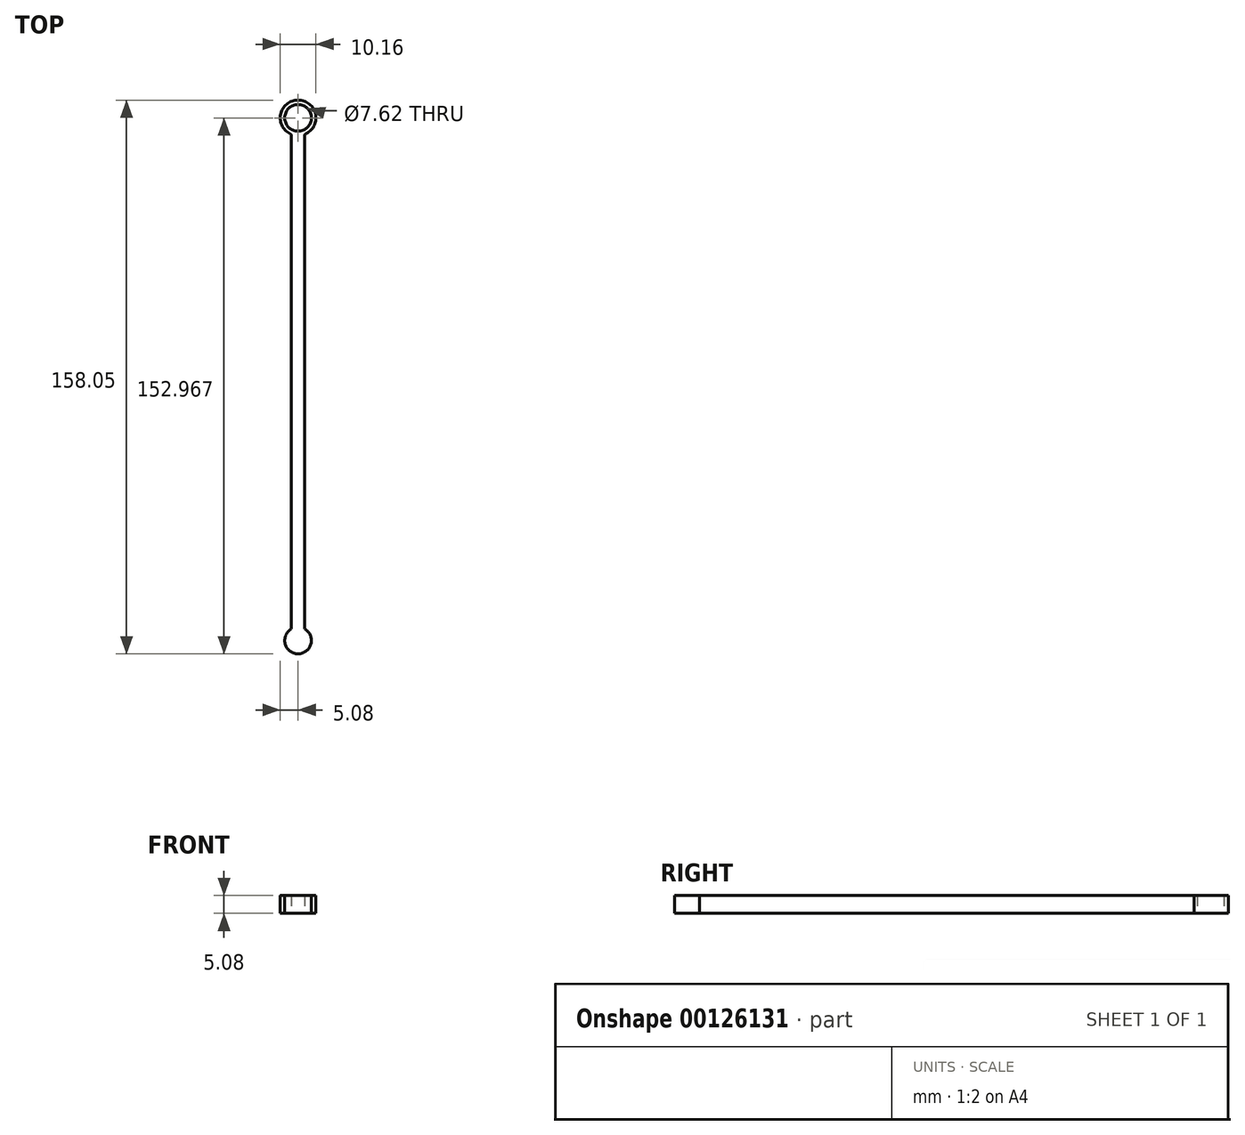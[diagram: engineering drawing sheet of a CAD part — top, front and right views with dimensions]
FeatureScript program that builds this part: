
annotation { "Feature Type Name" : "Feature", "Feature Type Description" : "" }
export const myFeature = defineFeature(function(context is Context, id is Id, definition is map)
    precondition{}
    {
        {
            var Q0;
            Q0=qCreatedBy(makeId("Top.planeOp"),FACE);
            var sketch = newSketch(context, id + "F0", { "sketchPlane" : qUnion([Q0])});
            skCircle(sketch, "E0", {"center": v(0, 45.97) * mm, "radius": 5.08 * mm});
            skLineSegment(sketch, "E1.bottom", {"start": v(-1.9, 40.32) * mm, "end": v(1.9, 40.32) * mm});
            skLineSegment(sketch, "E1.top", {"start": v(-1.9, -99.38) * mm, "end": v(1.9, -99.38) * mm});
            skLineSegment(sketch, "E1.left", {"start": v(-1.9, 40.32) * mm, "end": v(-1.9, -99.38) * mm});
            skLineSegment(sketch, "E1.right", {"start": v(1.9, 40.32) * mm, "end": v(1.9, -99.38) * mm});
            skCircle(sketch, "E2", {"center": v(0, 45.97) * mm, "radius": 3.81 * mm});
            skCircle(sketch, "E3", {"center": v(0, -103.2) * mm, "radius": 3.81 * mm});
            skLineSegment(sketch, "E4", {"start": v(-1.9, -99.38) * mm, "end": v(-1.9, -99.9) * mm});
            skLineSegment(sketch, "E5", {"start": v(1.9, -99.38) * mm, "end": v(1.9, -99.9) * mm});
            skLineSegment(sketch, "E6", {"start": v(-1.9, 40.32) * mm, "end": v(-1.9, 41.26) * mm});
            skLineSegment(sketch, "E7", {"start": v(1.9, 40.32) * mm, "end": v(1.9, 41.26) * mm});
            skSolve(sketch);
        }
        {
            var Q0;
            Q0=makeQuery(id+"F0.imprint","IMPRINT",FACE,{"disambiguationData":[TD([[makeQuery(id+"F0.imprint","IMPRINT",EDGE,{"derivedFrom":sQuery(id+"F0.wireOp",EDGE,"E2")}),-1.0]])]});
            var Q1;
            Q1=makeQuery(id+"F0.imprint","IMPRINT",FACE,{"disambiguationData":[TD([[makeQuery(id+"F0.imprint","IMPRINT",EDGE,{"derivedFrom":sQuery(id+"F0.wireOp",EDGE,"E1.bottom")}),1.0]])]});
            var Q2;
            Q2=makeQuery(id+"F0.imprint","IMPRINT",FACE,{"disambiguationData":[TD([[makeQuery(id+"F0.imprint","IMPRINT",EDGE,{"derivedFrom":sQuery(id+"F0.wireOp",EDGE,"E1.bottom")}),-1.0]])]});
            var Q3;
            {var subQ0=sQuery(id+"F0.wireOp",EDGE,"E4");Q3=makeQuery(id+"F0.imprint","IMPRINT",FACE,{"disambiguationData":[TD([[makeQuery(id+"F0.imprint","IMPRINT",EDGE,{"derivedFrom":subQ0}),1.0]])]});}
            var Q4;
            {var subQ0=sQuery(id+"F0.wireOp",EDGE,"E5");Q4=makeQuery(id+"F0.imprint","IMPRINT",FACE,{"disambiguationData":[TD([[makeQuery(id+"F0.imprint","IMPRINT",EDGE,{"derivedFrom":subQ0}),-1.0]])]});}
            var Q5;
            {var subQ0=sQuery(id+"F0.wireOp",EDGE,"E3");var subQ1=makeQuery(id+"F0.imprint","INTERSECT",VERTEX,{"derivedFrom":[subQ0,sQuery(id+"F0.wireOp",EDGE,"E5")]});Q5=makeQuery(id+"F0.imprint","IMPRINT",FACE,{"disambiguationData":[TD([[makeQuery(id+"F0.imprint","IMPRINT",EDGE,{"disambiguationData":[TD([[subQ1,-1.0]])],"derivedFrom":subQ0}),1.0]])]});}
            extrude(context, id + "F1", {"entities" : qUnion([Q0, Q1, Q2, Q3, Q4, Q5]), "depth" : 5.08 * mm});
        }
    });
